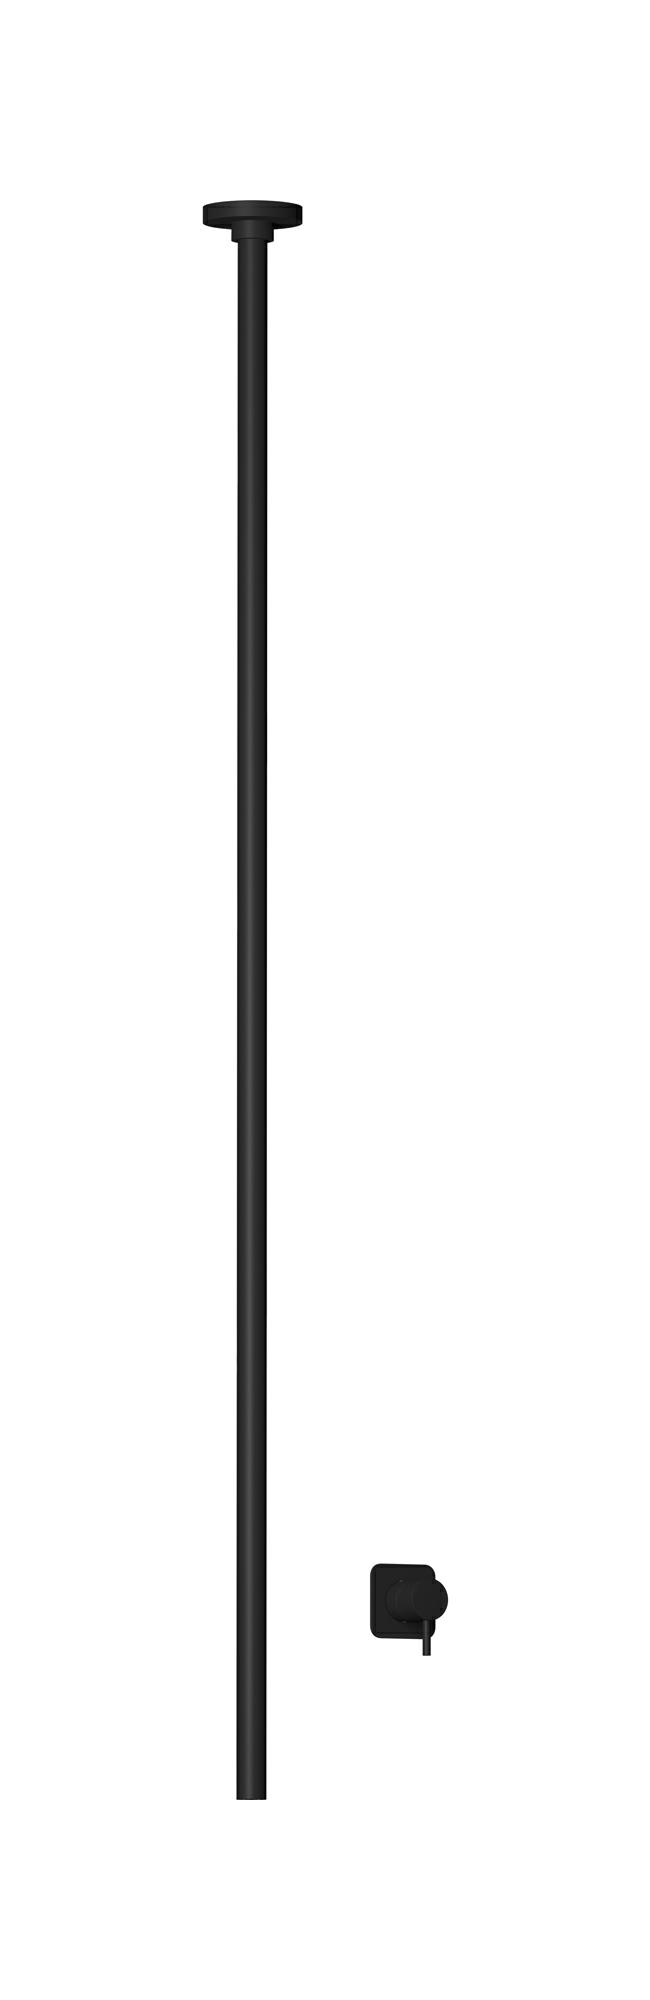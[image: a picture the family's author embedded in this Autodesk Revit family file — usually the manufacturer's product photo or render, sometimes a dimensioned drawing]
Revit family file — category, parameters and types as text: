
# Revit family: MT210
name_source: partatom
category: Apparecchi idraulici
units: mm (PartAtom-declared; Revit-internal decimal feet)

## family parameters
Basato su piano di lavoro = No
Condiviso = No
Mantieni orientamento annotazione = No
Numero OmniClass = 23.45.55.17
Punto di calcolo locali = No
Quota connettore circolare = Usa diametro
Sempre verticale = Sì
Taglio con vuoti quando caricato = No
Tipo di parte = Normale
Titolo OmniClass = Mixing Faucets

## types (3) — shared parameters
Cold water inlet = 10 mm  [stored 0.0328084 ft]
Commenti sul tipo = Spout
Connessione CW = No
Connessione HW = No
Connessione di scarico = No
Connessione di ventilazione = No
Descrizione = Ceiling spout with wall mounted mixer
Hot water inlet = 10 mm  [stored 0.0328084 ft]
Produttore = IB Rubinetterie S.p.A.
URL = https://www.weareib.it
zero-valued in all types: Prospetto di default

## per-type parameters (varying)
| type | Finishes surface | Immagine tipo | Modello |
| Chrome | IB_Chrome | MT210CC.jpg | MT210CC |
| Matt white | IB_matt white | MT210BO.jpg | MT210BO |
| Matt black | IB_matt black | MT210NP.jpg | MT210NP |

note: [stored X ft] marks values corroborated as IEEE doubles in the binary element streams (Revit-internal decimal feet)
